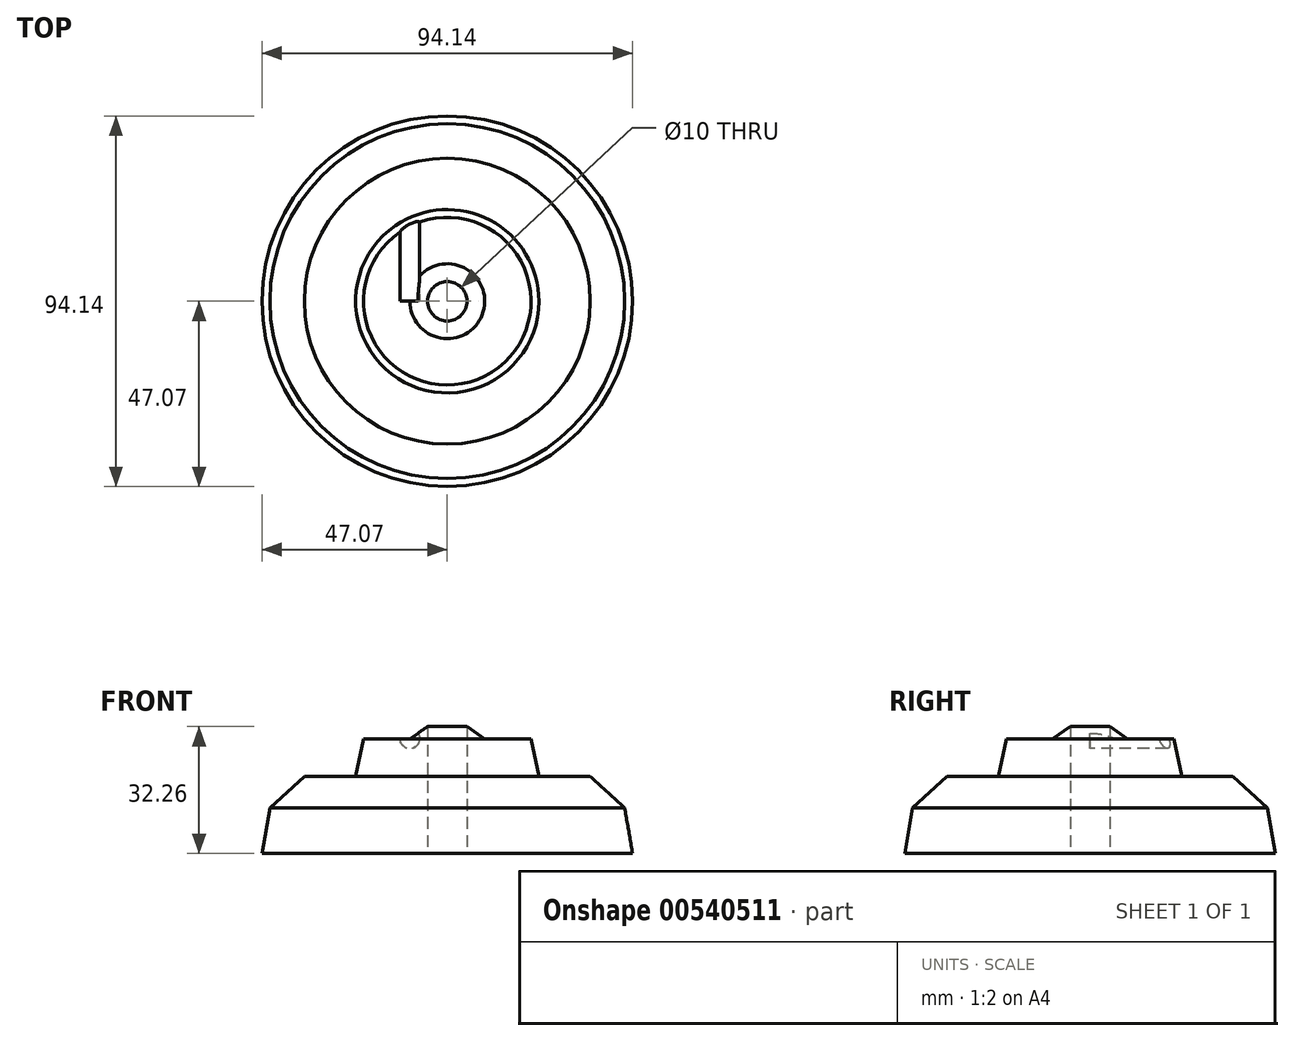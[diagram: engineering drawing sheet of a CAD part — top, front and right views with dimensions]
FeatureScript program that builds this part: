
annotation { "Feature Type Name" : "Feature", "Feature Type Description" : "" }
export const myFeature = defineFeature(function(context is Context, id is Id, definition is map)
    precondition{}
    {
        {
            var Q0;
            Q0=qCreatedBy(makeId("Front.planeOp"),FACE);
            var sketch = newSketch(context, id + "F0", { "sketchPlane" : qUnion([Q0])});
            skLineSegment(sketch, "E0", {"start": v(0, 35.68) * mm, "end": v(0, 0) * mm});
            skLineSegment(sketch, "E1", {"start": v(0, 0) * mm, "end": v(-47.07, 0) * mm});
            skLineSegment(sketch, "E2", {"start": v(-47.07, 0) * mm, "end": v(-45.07, 11.64) * mm});
            skLineSegment(sketch, "E3", {"start": v(-45.07, 11.64) * mm, "end": v(-36.3, 19.66) * mm});
            skLineSegment(sketch, "E4", {"start": v(-36.3, 19.66) * mm, "end": v(-23.29, 19.66) * mm});
            skLineSegment(sketch, "E5", {"start": v(-23.29, 19.66) * mm, "end": v(-21.28, 29.17) * mm});
            skLineSegment(sketch, "E6", {"start": v(-21.28, 29.17) * mm, "end": v(-9.52, 29.17) * mm});
            skLineSegment(sketch, "E7", {"start": v(-9.52, 29.17) * mm, "end": v(0, 35.68) * mm});
            skSolve(sketch);
        }
        {
            var Q0;
            Q0=makeQuery(id+"F0.imprint","IMPRINT",FACE,{"disambiguationData":[TD([[makeQuery(id+"F0.imprint","IMPRINT",EDGE,{"derivedFrom":sQuery(id+"F0.wireOp",EDGE,"E0")}),-1.0]])]});
            var Q1;
            Q1=sQuery(id+"F0.wireOp",EDGE,"E0");
            revolve(context, id + "F1", {"entities" : qUnion([Q0]), "axis" : qUnion([Q1]), "revolveType" : RevolveType.FULL});
        }
        {
            var Q0;
            Q0=makeQuery(id+"F1.opRevolve","SWEPT_FACE",FACE,{"disambiguationData":[OSD([sQuery(id+"F0.wireOp",EDGE,"E1")])]});
            var sketch = newSketch(context, id + "F2", { "sketchPlane" : qUnion([Q0])});
            skCircle(sketch, "E8", {"center": v(0, 0) * mm, "radius": 11.34 * mm});
            skCircle(sketch, "E9", {"center": v(0, 0) * mm, "radius": 47.07 * mm});
            skSolve(sketch);
        }
        {
            var Q0;
            Q0=sQuery(id+"F0.wireOp",VERTEX,"E7.end");
            var Q1;
            Q1=sQuery(id+"F0.wireOp",VERTEX,"E7.start");
            var Q2;
            Q2=makeQuery(id+"F1.opRevolve","SWEPT_BODY",BODY,{"disambiguationData":[OSD([sQuery(id+"F0.wireOp",EDGE,"E0"),sQuery(id+"F0.wireOp",EDGE,"E1"),sQuery(id+"F0.wireOp",EDGE,"E2"),sQuery(id+"F0.wireOp",EDGE,"E3"),sQuery(id+"F0.wireOp",EDGE,"E4"),sQuery(id+"F0.wireOp",EDGE,"E5"),sQuery(id+"F0.wireOp",EDGE,"E6"),sQuery(id+"F0.wireOp",EDGE,"E7")])]});
            hole(context, id + "F3", {"style" : HoleStyle.SIMPLE, "endStyle" : HoleEndStyle.THROUGH, "holeDiameter" : 5 * mm, "isTappedThrough" : true, "tappedDepth" : 12 * mm, "tapClearance" : 3, "locations" : qUnion([Q0, Q1]), "scope" : qUnion([Q2])});
        }
        {
            var Q0;
            Q0=sQuery(id+"F2.wireOp",VERTEX,"E9.center");
            var Q1;
            Q1=makeQuery(id+"F1.opRevolve","SWEPT_BODY",BODY,{"disambiguationData":[OSD([sQuery(id+"F0.wireOp",EDGE,"E0"),sQuery(id+"F0.wireOp",EDGE,"E1"),sQuery(id+"F0.wireOp",EDGE,"E2"),sQuery(id+"F0.wireOp",EDGE,"E3"),sQuery(id+"F0.wireOp",EDGE,"E4"),sQuery(id+"F0.wireOp",EDGE,"E5"),sQuery(id+"F0.wireOp",EDGE,"E6"),sQuery(id+"F0.wireOp",EDGE,"E7")])]});
            hole(context, id + "F4", {"style" : HoleStyle.SIMPLE, "endStyle" : HoleEndStyle.THROUGH, "holeDiameter" : 10 * mm, "isTappedThrough" : true, "tappedDepth" : 12 * mm, "tapClearance" : 3, "locations" : qUnion([Q0]), "scope" : qUnion([Q1])});
        }
    });
